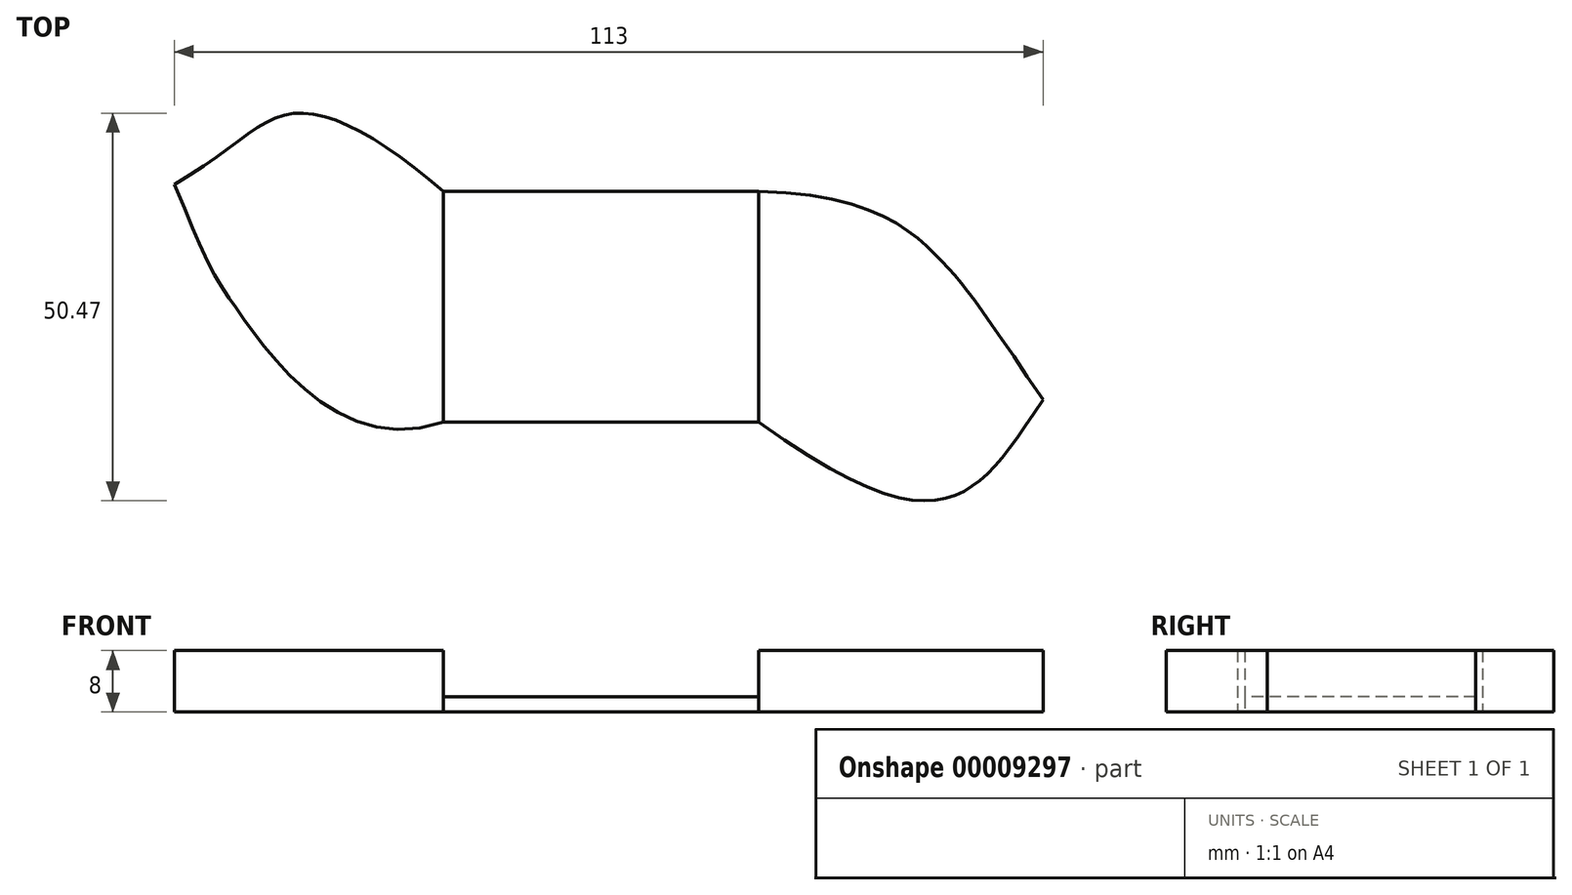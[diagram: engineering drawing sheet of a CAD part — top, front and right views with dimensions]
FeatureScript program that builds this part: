
annotation { "Feature Type Name" : "Feature", "Feature Type Description" : "" }
export const myFeature = defineFeature(function(context is Context, id is Id, definition is map)
    precondition{}
    {
        {
            var Q0;
            Q0=qCreatedBy(makeId("Top.planeOp"),FACE);
            var sketch = newSketch(context, id + "F0", { "sketchPlane" : qUnion([Q0])});
            skLineSegment(sketch, "E0", {"start": v(0, 0) * mm, "end": v(20, 0) * mm, "construction": true});
            skLineSegment(sketch, "E1", {"start": v(20, 0) * mm, "end": v(20, 15) * mm, "construction": true});
            skLineSegment(sketch, "E2.bottom", {"start": v(20, 15) * mm, "end": v(-21, 15) * mm});
            skLineSegment(sketch, "E2.top", {"start": v(20, -15) * mm, "end": v(-21, -15) * mm});
            skLineSegment(sketch, "E2.left", {"start": v(20, 15) * mm, "end": v(20, -15) * mm});
            skLineSegment(sketch, "E2.right", {"start": v(-21, 15) * mm, "end": v(-21, -15) * mm});
            skFitSpline(sketch, "E3", {"points": [v(-21, 15) * mm, v(-40.67, 25.14) * mm, v(-56, 15.93) * mm], "startDerivative": vector(-45.3, 38.84) * mm, "endDerivative": vector(-48.8, -28.18) * mm});
            skFitSpline(sketch, "E4", {"points": [v(-56, 15.93) * mm, v(-48.08, 0) * mm, v(-21, -15) * mm], "startDerivative": vector(33.1, -80.3) * mm, "endDerivative": vector(72.18, 25.04) * mm});
            skFitSpline(sketch, "E5", {"points": [v(20, 15) * mm, v(43.67, 6.1) * mm, v(57, -12.12) * mm], "startDerivative": vector(86.14, -1.7) * mm, "endDerivative": vector(50.36, -74.86) * mm});
            skFitSpline(sketch, "E6", {"points": [v(57, -12.12) * mm, v(46.96, -23.87) * mm, v(20, -15) * mm], "startDerivative": vector(-28.63, -42.7) * mm, "endDerivative": vector(-80.68, 58.32) * mm});
            skSolve(sketch);
        }
        {
            var Q0;
            Q0=makeQuery(id+"F0.imprint","IMPRINT",FACE,{"disambiguationData":[TD([[makeQuery(id+"F0.imprint","IMPRINT",EDGE,{"derivedFrom":sQuery(id+"F0.wireOp",EDGE,"E2.bottom")}),1.0]])]});
            extrude(context, id + "F1", {"entities" : qUnion([Q0]), "offsetDistance" : 25 * mm, "depth" : 2 * mm});
        }
        {
            var Q0;
            Q0=makeQuery(id+"F0.imprint","IMPRINT",FACE,{"disambiguationData":[TD([[makeQuery(id+"F0.imprint","IMPRINT",EDGE,{"derivedFrom":sQuery(id+"F0.wireOp",EDGE,"E2.right")}),-1.0]])]});
            var Q1;
            Q1=makeQuery(id+"F0.imprint","IMPRINT",FACE,{"disambiguationData":[TD([[makeQuery(id+"F0.imprint","IMPRINT",EDGE,{"derivedFrom":sQuery(id+"F0.wireOp",EDGE,"E2.left")}),1.0]])]});
            extrude(context, id + "F2", {"entities" : qUnion([Q0, Q1]), "operationType" : NewBodyOperationType.ADD, "offsetDistance" : 25 * mm, "depth" : 8 * mm});
        }
    });
